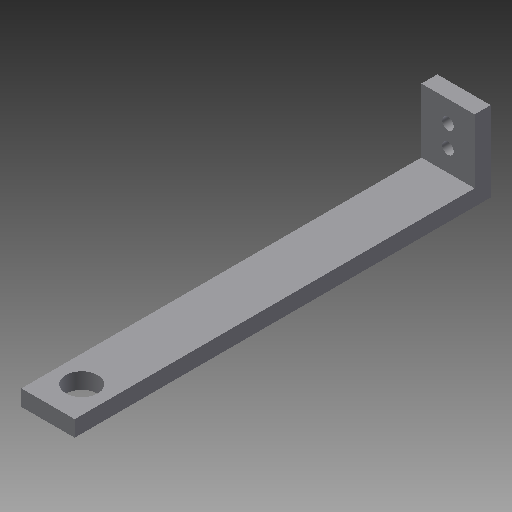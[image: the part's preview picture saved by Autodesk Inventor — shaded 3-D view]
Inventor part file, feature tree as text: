
AUTODESK INVENTOR PART (.ipt)
format: ipt  version: 2017 (Build 210142000, 142)  size: 104,448 bytes
history: native  units: in
note: dims shown in document units (in); Inventor stores cm internally (conversion verified against a paired STEP export)
features: sketch x2, extrude x2, hole x1
ambient origin geometry x8: Origin, YZ Plane, XZ Plane, XY Plane, X Axis, Y Axis, Z Axis, Center Point
bodies: Solid1 (feature_tree)
feature tree (5):
  sketch  "Sketch1"  dims[d0=0.3937in d1=3.0709in]
  extrude  "Extrusion1"  Depth=3.0709in
  extrude  "Extrusion2"  Depth=0.1181in
  hole  "Hole1"  [1 undecoded]
  sketch  "Sketch2"  dims[d2=0.2494in d3=0.1181in d4=0.1181in d5=0.0in d6=0.5906in d7=0.0in d8=0.1575in d9=0.0866in d10=0.2362in d11=0.1575in d12=0.0787in d13=90.0deg d14=0.315in d15=0.8108in d16=0.2362in]
note: 1 required parameter value undecoded (feature->parameter linkage not recoverable at this tier; creation-order binding heuristic only, values carry confidence <= 0.55)
